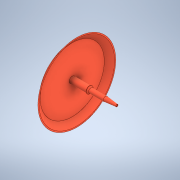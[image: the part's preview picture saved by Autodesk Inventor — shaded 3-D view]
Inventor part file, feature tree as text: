
AUTODESK INVENTOR PART (.ipt)
format: ipt  version: 2020 (Build 240168000, 168)  size: 205,312 bytes
history: native  units: mm
features: sketch x11, extrude x8, fillet x3, revolve x2, plane x1, chamfer x1
ambient origin geometry x8: Origin, YZ Plane, XZ Plane, XY Plane, X Axis, Y Axis, Z Axis, Center Point
bodies: Solid1 (feature_tree)
feature tree (26):
  extrude  "Extrusion1"  Depth=28.0mm
  plane  "Work Plane1"
  sketch  "Sketch2"  dims[d2=0.4mm d3=0.0mm d4=2.0mm]
  revolve  "Revolution1"  [1 undecoded]
  extrude  "Extrusion2"  TaperAngle=90.0deg  [1 undecoded]
  fillet  "Fillet1"  Radius=9.0mm
  extrude  "Extrusion3"  Depth=2.0mm
  extrude  "Extrusion4"  Depth=3.0mm TaperAngle=0.0deg
  extrude  "Extrusion5"  Depth=7.5mm TaperAngle=0.0deg
  extrude  "Extrusion6"  Depth=3.0mm TaperAngle=0.0deg
  chamfer  "Chamfer1"  Distance=11.86mm
  revolve  "Revolution2"  [1 undecoded]
  extrude  "Extrusion7"  TaperAngle=90.0deg  [1 undecoded]
  fillet  "Fillet2"  Radius=0.8mm
  extrude  "Extrusion8"  Depth=0.1mm
  fillet  "Fillet3"  Radius=6.5mm
  sketch  "Sketch1"  dims[d0=34.0mm d1=28.0mm]
  sketch  "Sketch3"  dims[d5=34.0mm d6=90.0deg d7=9.0mm]
  sketch  "Sketch4"  dims[d8=0.6mm d9=0.0mm d10=2.0mm]
  sketch  "Sketch5"  dims[d11=2.0mm d12=3.0mm d13=0.0mm]
  sketch  "Sketch6"  dims[d14=2.7mm d15=7.5mm d16=0.0mm]
  sketch  "Sketch7"  dims[d17=3.0mm d18=0.14mm d19=0.0mm]
  sketch  "Sketch8"  dims[d20=2.0mm d21=11.86mm d22=0.0mm]
  sketch  "Sketch9"  dims[d23=0.5mm d24=2.0mm d25=45.0deg d26=0.5mm]
  sketch  "Sketch10"  dims[d27=5.0mm d28=90.0deg d29=0.8mm]
  sketch  "Sketch11"  dims[d30=0.1mm d31=0.0mm d32=0.1mm d33=6.5mm d34=0.1mm d35=0.0mm d36=0.1mm]
note: 4 required parameter values undecoded (feature->parameter linkage not recoverable at this tier; creation-order binding heuristic only, values carry confidence <= 0.55)